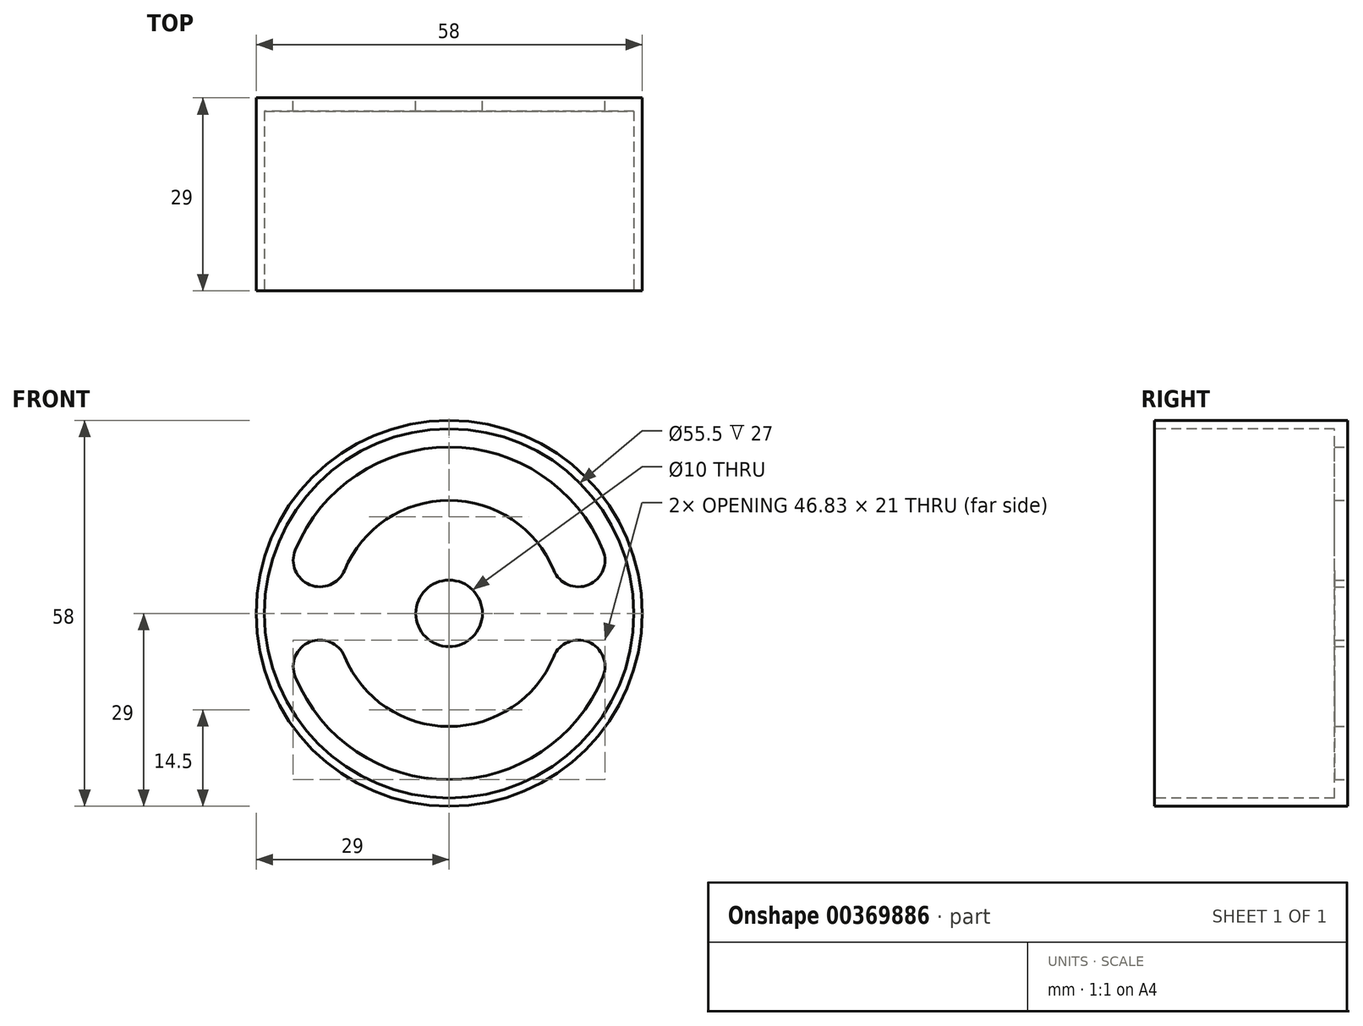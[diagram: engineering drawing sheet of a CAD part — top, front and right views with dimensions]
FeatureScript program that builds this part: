
annotation { "Feature Type Name" : "Feature", "Feature Type Description" : "" }
export const myFeature = defineFeature(function(context is Context, id is Id, definition is map)
    precondition{}
    {
        {
            var Q0;
            Q0=qCreatedBy(makeId("Front.planeOp"),FACE);
            var sketch = newSketch(context, id + "F0", { "sketchPlane" : qUnion([Q0])});
            skCircle(sketch, "E0", {"center": v(0, 0) * mm, "radius": 29 * mm});
            skSolve(sketch);
        }
        {
            var Q0;
            Q0=makeQuery(id+"F0.imprint","IMPRINT",FACE,{"disambiguationData":[TD([[makeQuery(id+"F0.imprint","IMPRINT",EDGE,{"derivedFrom":sQuery(id+"F0.wireOp",EDGE,"E0")}),1.0]])]});
            extrude(context, id + "F1", {"entities" : qUnion([Q0]), "depth" : 29 * mm});
        }
        {
            var Q0;
            Q0=makeQuery(id+"F1.opExtrude","CAP_FACE",FACE,{"disambiguationData":[OSD([sQuery(id+"F0.wireOp",EDGE,"E0")])],"isStart":false});
            var sketch = newSketch(context, id + "F2", { "sketchPlane" : qUnion([Q0])});
            skCircle(sketch, "E1", {"center": v(0, 0) * mm, "radius": 27.75 * mm});
            skSolve(sketch);
        }
        {
            var Q0;
            Q0=makeQuery(id+"F2.imprint","IMPRINT",FACE,{"disambiguationData":[TD([[makeQuery(id+"F2.imprint","IMPRINT",EDGE,{"derivedFrom":sQuery(id+"F2.wireOp",EDGE,"E1")}),1.0]])]});
            extrude(context, id + "F3", {"entities" : qUnion([Q0]), "operationType" : NewBodyOperationType.REMOVE, "oppositeDirection" : true, "depth" : 27 * mm});
        }
        {
            var Q0;
            Q0=makeQuery(id+"F1.opExtrude","CAP_FACE",FACE,{"disambiguationData":[OSD([sQuery(id+"F0.wireOp",EDGE,"E0")])],"isStart":true});
            var sketch = newSketch(context, id + "F4", { "sketchPlane" : qUnion([Q0])});
            skArc(sketch, "E2", {"start": v(-23.11, -9.52) * mm, "mid": v(0, -25) * mm, "end": v(23.11, -9.52) * mm});
            skArc(sketch, "E3", {"start": v(-15.72, -6.48) * mm, "mid": v(0, -17) * mm, "end": v(15.72, -6.48) * mm});
            skArc(sketch, "E4", {"start": v(-20.58, -4.17) * mm, "mid": v(-20.1, -6.11) * mm, "end": v(-19.42, -8) * mm, "construction": true});
            skArc(sketch, "E5", {"start": v(-23.11, 9.52) * mm, "mid": v(-20.94, 4.3) * mm, "end": v(-15.72, 6.48) * mm});
            skArc(sketch, "E6", {"start": v(15.72, 6.48) * mm, "mid": v(20.94, 4.3) * mm, "end": v(23.11, 9.52) * mm});
            skArc(sketch, "E7", {"start": v(-15.72, -6.48) * mm, "mid": v(-20.94, -4.3) * mm, "end": v(-23.11, -9.52) * mm});
            skArc(sketch, "E8", {"start": v(23.11, -9.52) * mm, "mid": v(20.94, -4.3) * mm, "end": v(15.72, -6.48) * mm});
            skArc(sketch, "E9.trimOffspring", {"start": v(-19.42, 8) * mm, "mid": v(-20.1, 6.11) * mm, "end": v(-20.58, 4.17) * mm, "construction": true});
            skArc(sketch, "E10.trimOffspring", {"start": v(17.55, -11.54) * mm, "mid": v(19.42, -8) * mm, "end": v(20.58, -4.17) * mm, "construction": true});
            skArc(sketch, "E11.trimOffspring", {"start": v(15.72, 6.48) * mm, "mid": v(0, 17) * mm, "end": v(-15.72, 6.48) * mm});
            skArc(sketch, "E12.trimOffspring", {"start": v(23.11, 9.52) * mm, "mid": v(0, 25) * mm, "end": v(-23.11, 9.52) * mm});
            skArc(sketch, "E13.trimOffspring", {"start": v(20.58, 4.17) * mm, "mid": v(20.1, 6.11) * mm, "end": v(19.42, 8) * mm, "construction": true});
            skSolve(sketch);
        }
        {
            var Q0;
            Q0 = qSketchRegion(id + "F4", true);
            extrude(context, id + "F5", {"entities" : qUnion([Q0]), "operationType" : NewBodyOperationType.REMOVE, "oppositeDirection" : true, "depth" : 2 * mm});
        }
        {
            var Q0;
            Q0=makeQuery(id+"F1.opExtrude","CAP_FACE",FACE,{"disambiguationData":[OSD([sQuery(id+"F0.wireOp",EDGE,"E0")])],"isStart":true});
            var sketch = newSketch(context, id + "F6", { "sketchPlane" : qUnion([Q0])});
            skCircle(sketch, "E14", {"center": v(0, 0) * mm, "radius": 5 * mm});
            skSolve(sketch);
        }
        {
            var Q0;
            Q0=makeQuery(id+"F6.imprint","IMPRINT",FACE,{"disambiguationData":[TD([[makeQuery(id+"F6.imprint","IMPRINT",EDGE,{"derivedFrom":sQuery(id+"F6.wireOp",EDGE,"E14")}),1.0]])]});
            extrude(context, id + "F7", {"entities" : qUnion([Q0]), "operationType" : NewBodyOperationType.REMOVE, "oppositeDirection" : true, "depth" : 2 * mm});
        }
    });
